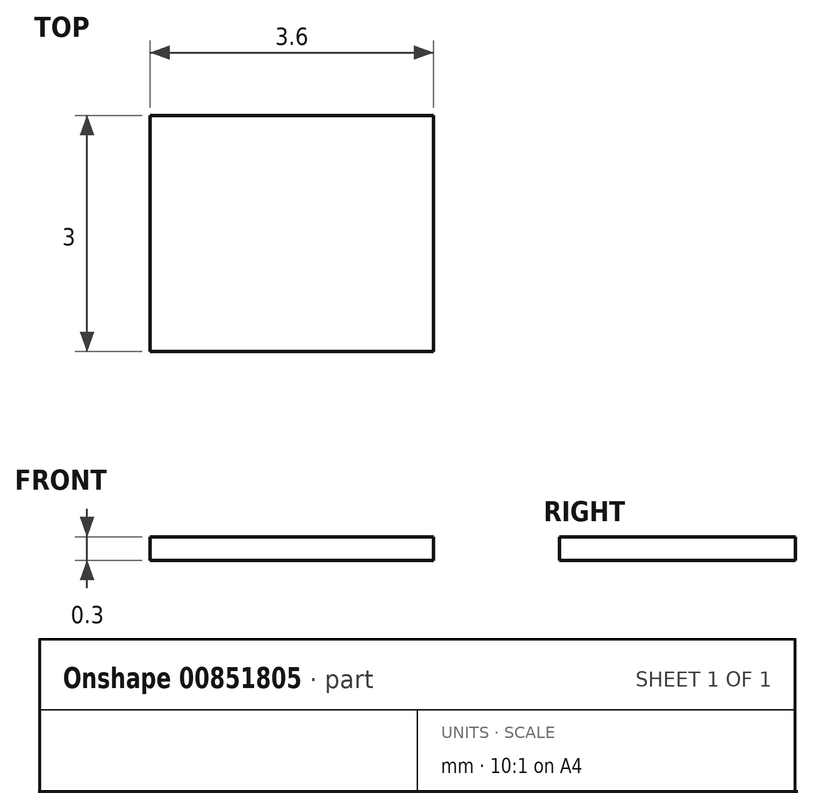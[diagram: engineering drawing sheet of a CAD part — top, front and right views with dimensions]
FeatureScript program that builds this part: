
annotation { "Feature Type Name" : "Feature", "Feature Type Description" : "" }
export const myFeature = defineFeature(function(context is Context, id is Id, definition is map)
    precondition{}
    {
        {
            var Q0;
            Q0=qCreatedBy(makeId("Front.planeOp"),FACE);
            var sketch = newSketch(context, id + "F0", { "sketchPlane" : qUnion([Q0])});
            skLineSegment(sketch, "E0.bottom", {"start": v(0, 0) * mm, "end": v(3.6, 0) * mm});
            skLineSegment(sketch, "E0.top", {"start": v(0, 0.3) * mm, "end": v(3.6, 0.3) * mm});
            skLineSegment(sketch, "E0.left", {"start": v(0, 0) * mm, "end": v(0, 0.3) * mm});
            skLineSegment(sketch, "E0.right", {"start": v(3.6, 0) * mm, "end": v(3.6, 0.3) * mm});
            skSolve(sketch);
        }
        {
            var Q0;
            Q0 = qSketchRegion(id + "F0", true);
            extrude(context, id + "F1", {"entities" : qUnion([Q0]), "depth" : 3 * mm, "offsetDistance" : 25.4 * mm});
        }
    });
